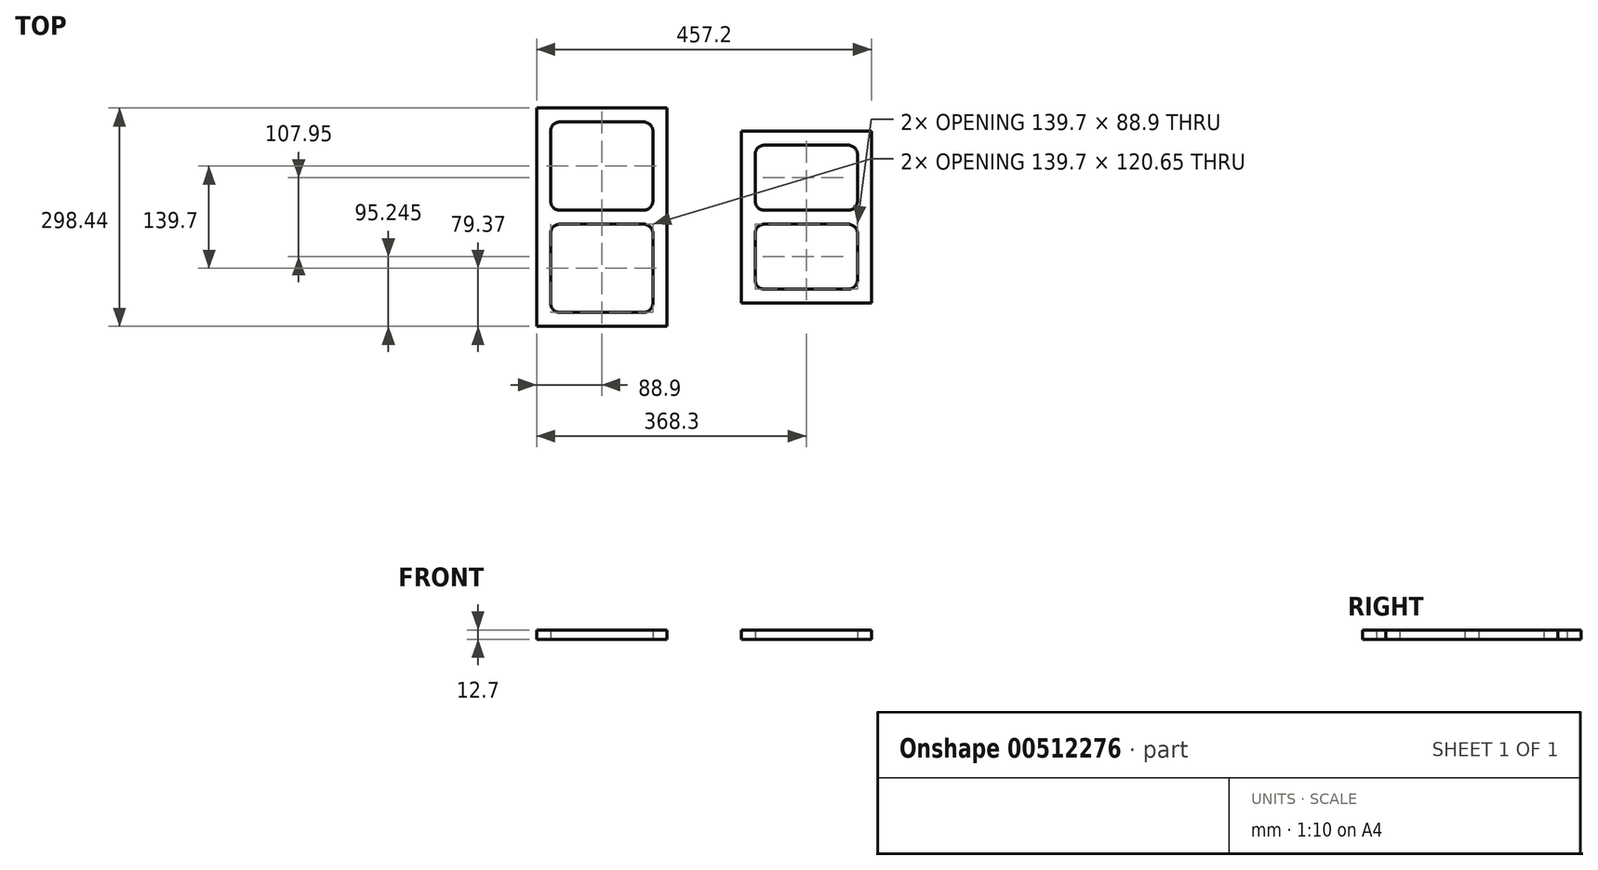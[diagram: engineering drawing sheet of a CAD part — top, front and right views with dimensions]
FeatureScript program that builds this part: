
annotation { "Feature Type Name" : "Feature", "Feature Type Description" : "" }
export const myFeature = defineFeature(function(context is Context, id is Id, definition is map)
    precondition{}
    {
        {
            var Q0;
            Q0=qCreatedBy(makeId("Top.planeOp"),FACE);
            var sketch = newSketch(context, id + "F0", { "sketchPlane" : qUnion([Q0])});
            skLineSegment(sketch, "E0.bottom", {"start": v(-88.9, 149.23) * mm, "end": v(88.9, 149.22) * mm});
            skLineSegment(sketch, "E0.top", {"start": v(-88.9, -149.22) * mm, "end": v(88.9, -149.23) * mm});
            skLineSegment(sketch, "E0.left", {"start": v(-88.9, 149.22) * mm, "end": v(-88.9, -149.22) * mm});
            skLineSegment(sketch, "E0.right", {"start": v(88.9, 149.22) * mm, "end": v(88.9, -149.22) * mm});
            skLineSegment(sketch, "E1.bottom", {"start": v(-69.85, 130.18) * mm, "end": v(69.85, 130.17) * mm});
            skLineSegment(sketch, "E1.top", {"start": v(-69.85, 9.52) * mm, "end": v(69.85, 9.52) * mm});
            skLineSegment(sketch, "E1.left", {"start": v(-69.85, 130.18) * mm, "end": v(-69.85, 9.52) * mm});
            skLineSegment(sketch, "E1.right", {"start": v(69.85, 130.18) * mm, "end": v(69.85, 9.53) * mm});
            skLineSegment(sketch, "E2.bottom", {"start": v(-69.85, -9.52) * mm, "end": v(69.85, -9.52) * mm});
            skLineSegment(sketch, "E2.top", {"start": v(-69.85, -130.18) * mm, "end": v(69.85, -130.18) * mm});
            skLineSegment(sketch, "E2.left", {"start": v(-69.85, -9.52) * mm, "end": v(-69.85, -130.18) * mm});
            skLineSegment(sketch, "E2.right", {"start": v(69.85, -9.53) * mm, "end": v(69.85, -130.18) * mm});
            skArc(sketch, "E3", {"start": v(-57.15, 130.18) * mm, "mid": v(-66.13, 126.46) * mm, "end": v(-69.85, 117.48) * mm});
            skArc(sketch, "E4", {"start": v(69.85, 117.48) * mm, "mid": v(66.13, 126.46) * mm, "end": v(57.15, 130.18) * mm});
            skArc(sketch, "E5", {"start": v(57.15, 9.52) * mm, "mid": v(66.13, 13.24) * mm, "end": v(69.85, 22.22) * mm});
            skArc(sketch, "E6", {"start": v(-69.85, 22.22) * mm, "mid": v(-66.13, 13.24) * mm, "end": v(-57.15, 9.52) * mm});
            skArc(sketch, "E7", {"start": v(69.85, -22.22) * mm, "mid": v(66.13, -13.24) * mm, "end": v(57.15, -9.52) * mm});
            skArc(sketch, "E8", {"start": v(57.15, -130.18) * mm, "mid": v(66.13, -126.46) * mm, "end": v(69.85, -117.48) * mm});
            skArc(sketch, "E9", {"start": v(-69.85, -117.48) * mm, "mid": v(-66.13, -126.46) * mm, "end": v(-57.15, -130.18) * mm});
            skArc(sketch, "E10", {"start": v(-57.15, -9.52) * mm, "mid": v(-66.13, -13.24) * mm, "end": v(-69.85, -22.22) * mm});
            skLineSegment(sketch, "E11.bottom", {"start": v(190.5, -117.48) * mm, "end": v(368.3, -117.48) * mm});
            skLineSegment(sketch, "E11.top", {"start": v(190.5, 117.48) * mm, "end": v(368.3, 117.48) * mm});
            skLineSegment(sketch, "E11.left", {"start": v(190.5, -117.48) * mm, "end": v(190.5, 117.48) * mm});
            skLineSegment(sketch, "E11.right", {"start": v(368.3, -117.48) * mm, "end": v(368.3, 117.48) * mm});
            skLineSegment(sketch, "E12.bottom", {"start": v(209.55, -98.43) * mm, "end": v(349.25, -98.43) * mm});
            skLineSegment(sketch, "E12.top", {"start": v(209.55, -9.53) * mm, "end": v(349.25, -9.53) * mm});
            skLineSegment(sketch, "E12.left", {"start": v(209.55, -98.43) * mm, "end": v(209.55, -9.53) * mm});
            skLineSegment(sketch, "E12.right", {"start": v(349.25, -98.43) * mm, "end": v(349.25, -9.53) * mm});
            skLineSegment(sketch, "E13.bottom", {"start": v(209.55, 98.43) * mm, "end": v(349.25, 98.43) * mm});
            skLineSegment(sketch, "E13.top", {"start": v(209.55, 9.53) * mm, "end": v(349.25, 9.53) * mm});
            skLineSegment(sketch, "E13.left", {"start": v(209.55, 98.43) * mm, "end": v(209.55, 9.53) * mm});
            skLineSegment(sketch, "E13.right", {"start": v(349.25, 98.43) * mm, "end": v(349.25, 9.53) * mm});
            skArc(sketch, "E14", {"start": v(222.25, -9.53) * mm, "mid": v(213.27, -13.24) * mm, "end": v(209.55, -22.23) * mm});
            skArc(sketch, "E15", {"start": v(349.25, -22.23) * mm, "mid": v(345.53, -13.24) * mm, "end": v(336.55, -9.53) * mm});
            skArc(sketch, "E16", {"start": v(336.55, -98.43) * mm, "mid": v(345.53, -94.7) * mm, "end": v(349.25, -85.73) * mm});
            skArc(sketch, "E17", {"start": v(209.55, -85.73) * mm, "mid": v(213.27, -94.7) * mm, "end": v(222.25, -98.43) * mm});
            skArc(sketch, "E18", {"start": v(222.25, 98.43) * mm, "mid": v(213.27, 94.7) * mm, "end": v(209.55, 85.73) * mm});
            skArc(sketch, "E19", {"start": v(349.25, 85.73) * mm, "mid": v(345.53, 94.7) * mm, "end": v(336.55, 98.43) * mm});
            skArc(sketch, "E20", {"start": v(336.55, 9.53) * mm, "mid": v(345.53, 13.24) * mm, "end": v(349.25, 22.23) * mm});
            skArc(sketch, "E21", {"start": v(209.55, 22.23) * mm, "mid": v(213.27, 13.24) * mm, "end": v(222.25, 9.53) * mm});
            skSolve(sketch);
        }
        {
            var Q0;
            Q0=makeQuery(id+"F0.imprint","IMPRINT",FACE,{"disambiguationData":[TD([[makeQuery(id+"F0.imprint","IMPRINT",EDGE,{"derivedFrom":sQuery(id+"F0.wireOp",EDGE,"E0.bottom")}),-1.0]])]});
            var Q1;
            {var subQ3=sQuery(id+"F0.wireOp",EDGE,"E3");Q1=makeQuery(id+"F0.imprint","IMPRINT",FACE,{"disambiguationData":[TD([[makeQuery(id+"F0.imprint","IMPRINT",EDGE,{"derivedFrom":subQ3}),-1.0]])]});}
            var Q2;
            {var subQ3=sQuery(id+"F0.wireOp",EDGE,"E4");Q2=makeQuery(id+"F0.imprint","IMPRINT",FACE,{"disambiguationData":[TD([[makeQuery(id+"F0.imprint","IMPRINT",EDGE,{"derivedFrom":subQ3}),-1.0]])]});}
            var Q3;
            {var subQ3=sQuery(id+"F0.wireOp",EDGE,"E5");Q3=makeQuery(id+"F0.imprint","IMPRINT",FACE,{"disambiguationData":[TD([[makeQuery(id+"F0.imprint","IMPRINT",EDGE,{"derivedFrom":subQ3}),-1.0]])]});}
            var Q4;
            {var subQ3=sQuery(id+"F0.wireOp",EDGE,"E6");Q4=makeQuery(id+"F0.imprint","IMPRINT",FACE,{"disambiguationData":[TD([[makeQuery(id+"F0.imprint","IMPRINT",EDGE,{"derivedFrom":subQ3}),-1.0]])]});}
            var Q5;
            {var subQ3=sQuery(id+"F0.wireOp",EDGE,"E10");Q5=makeQuery(id+"F0.imprint","IMPRINT",FACE,{"disambiguationData":[TD([[makeQuery(id+"F0.imprint","IMPRINT",EDGE,{"derivedFrom":subQ3}),-1.0]])]});}
            var Q6;
            {var subQ3=sQuery(id+"F0.wireOp",EDGE,"E7");Q6=makeQuery(id+"F0.imprint","IMPRINT",FACE,{"disambiguationData":[TD([[makeQuery(id+"F0.imprint","IMPRINT",EDGE,{"derivedFrom":subQ3}),-1.0]])]});}
            var Q7;
            {var subQ3=sQuery(id+"F0.wireOp",EDGE,"E8");Q7=makeQuery(id+"F0.imprint","IMPRINT",FACE,{"disambiguationData":[TD([[makeQuery(id+"F0.imprint","IMPRINT",EDGE,{"derivedFrom":subQ3}),-1.0]])]});}
            var Q8;
            {var subQ3=sQuery(id+"F0.wireOp",EDGE,"E9");Q8=makeQuery(id+"F0.imprint","IMPRINT",FACE,{"disambiguationData":[TD([[makeQuery(id+"F0.imprint","IMPRINT",EDGE,{"derivedFrom":subQ3}),-1.0]])]});}
            extrude(context, id + "F1", {"entities" : qUnion([Q0, Q1, Q2, Q3, Q4, Q5, Q6, Q7, Q8]), "depth" : 12.7 * mm});
        }
        {
            var Q0;
            Q0=makeQuery(id+"F0.imprint","IMPRINT",FACE,{"disambiguationData":[TD([[makeQuery(id+"F0.imprint","IMPRINT",EDGE,{"derivedFrom":sQuery(id+"F0.wireOp",EDGE,"E11.bottom")}),1.0]])]});
            var Q1;
            {var subQ3=sQuery(id+"F0.wireOp",EDGE,"E18");Q1=makeQuery(id+"F0.imprint","IMPRINT",FACE,{"disambiguationData":[TD([[makeQuery(id+"F0.imprint","IMPRINT",EDGE,{"derivedFrom":subQ3}),-1.0]])]});}
            var Q2;
            {var subQ3=sQuery(id+"F0.wireOp",EDGE,"E19");Q2=makeQuery(id+"F0.imprint","IMPRINT",FACE,{"disambiguationData":[TD([[makeQuery(id+"F0.imprint","IMPRINT",EDGE,{"derivedFrom":subQ3}),-1.0]])]});}
            var Q3;
            {var subQ3=sQuery(id+"F0.wireOp",EDGE,"E20");Q3=makeQuery(id+"F0.imprint","IMPRINT",FACE,{"disambiguationData":[TD([[makeQuery(id+"F0.imprint","IMPRINT",EDGE,{"derivedFrom":subQ3}),-1.0]])]});}
            var Q4;
            {var subQ3=sQuery(id+"F0.wireOp",EDGE,"E21");Q4=makeQuery(id+"F0.imprint","IMPRINT",FACE,{"disambiguationData":[TD([[makeQuery(id+"F0.imprint","IMPRINT",EDGE,{"derivedFrom":subQ3}),-1.0]])]});}
            var Q5;
            {var subQ3=sQuery(id+"F0.wireOp",EDGE,"E14");Q5=makeQuery(id+"F0.imprint","IMPRINT",FACE,{"disambiguationData":[TD([[makeQuery(id+"F0.imprint","IMPRINT",EDGE,{"derivedFrom":subQ3}),-1.0]])]});}
            var Q6;
            {var subQ3=sQuery(id+"F0.wireOp",EDGE,"E15");Q6=makeQuery(id+"F0.imprint","IMPRINT",FACE,{"disambiguationData":[TD([[makeQuery(id+"F0.imprint","IMPRINT",EDGE,{"derivedFrom":subQ3}),-1.0]])]});}
            var Q7;
            {var subQ3=sQuery(id+"F0.wireOp",EDGE,"E16");Q7=makeQuery(id+"F0.imprint","IMPRINT",FACE,{"disambiguationData":[TD([[makeQuery(id+"F0.imprint","IMPRINT",EDGE,{"derivedFrom":subQ3}),-1.0]])]});}
            var Q8;
            {var subQ3=sQuery(id+"F0.wireOp",EDGE,"E17");Q8=makeQuery(id+"F0.imprint","IMPRINT",FACE,{"disambiguationData":[TD([[makeQuery(id+"F0.imprint","IMPRINT",EDGE,{"derivedFrom":subQ3}),-1.0]])]});}
            extrude(context, id + "F2", {"entities" : qUnion([Q0, Q1, Q2, Q3, Q4, Q5, Q6, Q7, Q8]), "depth" : 12.7 * mm});
        }
    });
